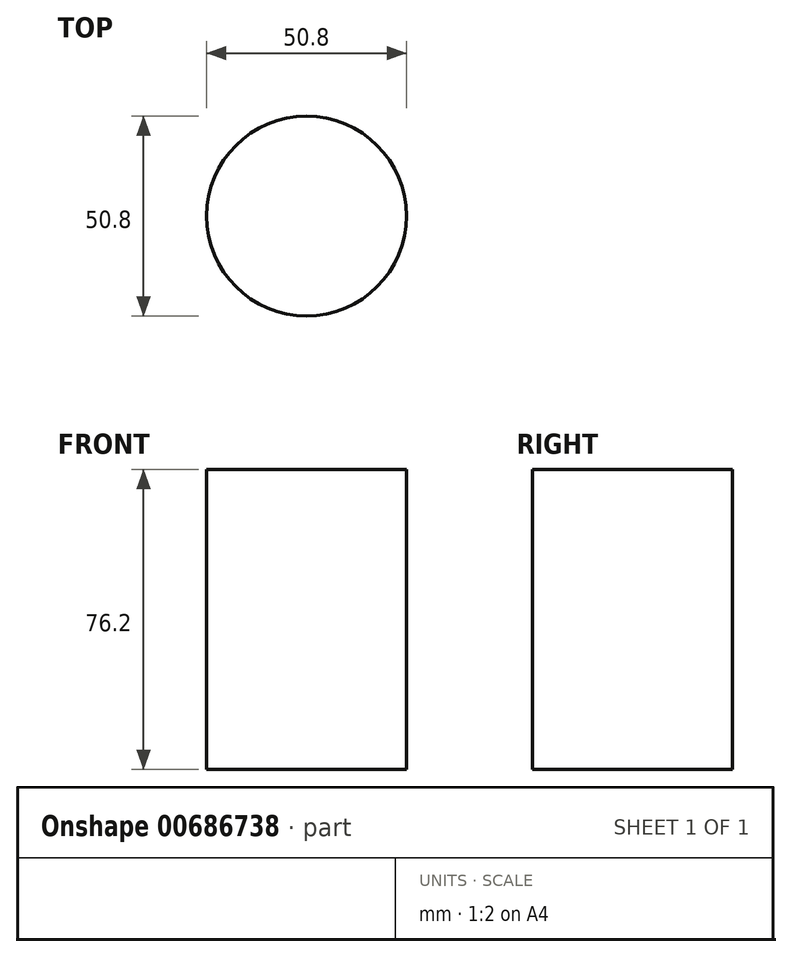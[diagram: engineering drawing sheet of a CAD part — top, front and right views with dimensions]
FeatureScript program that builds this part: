
annotation { "Feature Type Name" : "Feature", "Feature Type Description" : "" }
export const myFeature = defineFeature(function(context is Context, id is Id, definition is map)
    precondition{}
    {
        {
            var Q0;
            Q0=qCreatedBy(makeId("Top.planeOp"),FACE);
            var sketch = newSketch(context, id + "F0", { "sketchPlane" : qUnion([Q0])});
            skCircle(sketch, "E0", {"center": v(0, 0) * mm, "radius": 25.4 * mm});
            skSolve(sketch);
        }
        {
            var Q0;
            Q0=makeQuery(id+"F0.imprint","IMPRINT",FACE,{"disambiguationData":[TD([[makeQuery(id+"F0.imprint","IMPRINT",EDGE,{"derivedFrom":sQuery(id+"F0.wireOp",EDGE,"E0")}),1.0]])]});
            extrude(context, id + "F1", {"entities" : qUnion([Q0]), "depth" : 76.2 * mm, "offsetDistance" : 25.4 * mm});
        }
        {
            var Q0;
            Q0=makeQuery(id+"F1.opExtrude","CAP_FACE",FACE,{"disambiguationData":[OSD([sQuery(id+"F0.wireOp",EDGE,"E0")])],"isStart":false});
            var sketch = newSketch(context, id + "F2", { "sketchPlane" : qUnion([Q0])});
            skFitSpline(sketch, "E1", {"points": [v(-123.3, 0) * mm, v(-133.85, -18.61) * mm, v(-114.13, -37.2) * mm, v(-102.1, -34.48) * mm, v(-117.47, -25.2) * mm], "startDerivative": vector(-90.69, 0) * mm, "endDerivative": vector(-191.37, -33.94) * mm});
            skSolve(sketch);
        }
        {
            var Q0;
            Q0=sQuery(id+"F2.wireOp",EDGE,"E1");
            extrude(context, id + "F3", {"bodyType" : ToolBodyType.SURFACE, "surfaceEntities" : qUnion([Q0]), "depth" : 5.08 * mm, "offsetDistance" : 25.4 * mm});
        }
    });
